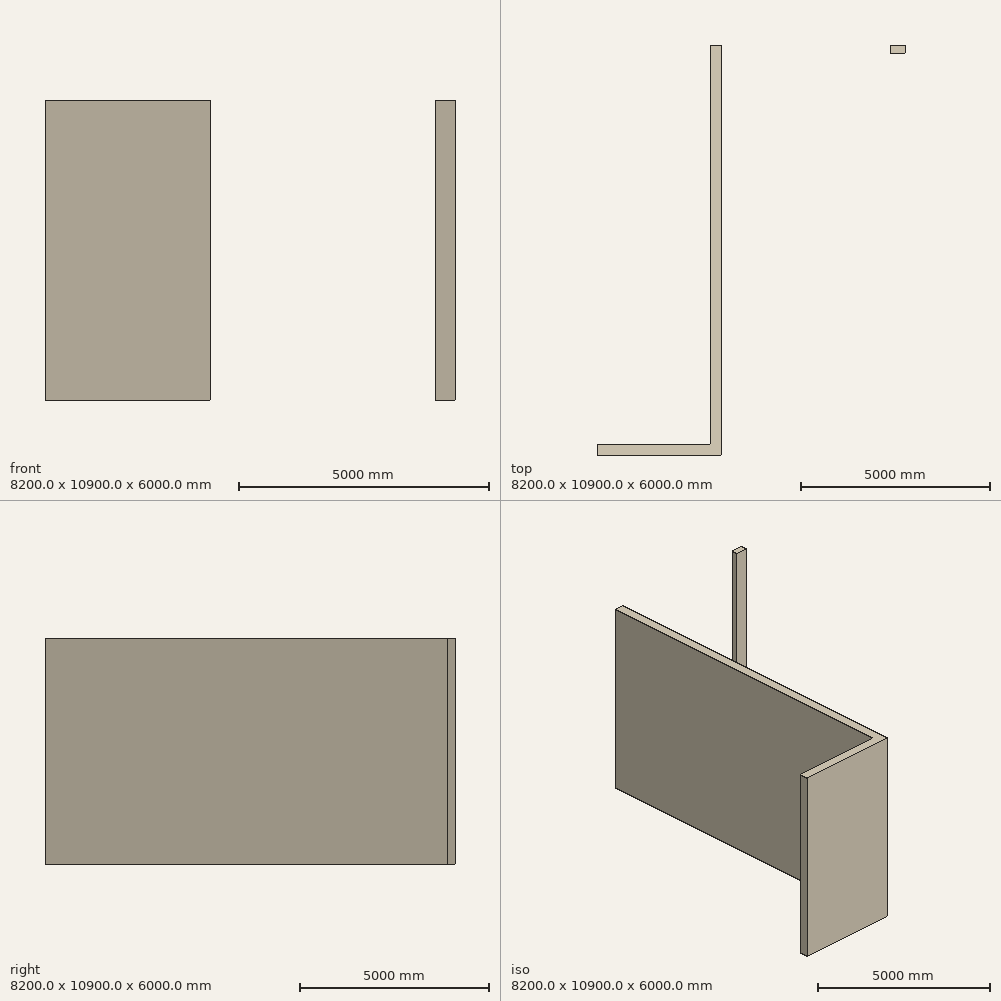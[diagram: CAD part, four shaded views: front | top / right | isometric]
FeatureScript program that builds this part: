
annotation { "Feature Type Name" : "Feature", "Feature Type Description" : "" }
export const myFeature = defineFeature(function(context is Context, id is Id, definition is map)
    precondition{}
    {
        {
            var Q0;
            Q0=qCreatedBy(makeId("Top.planeOp"),FACE);
            var sketch = newSketch(context, id + "F0", { "sketchPlane" : qUnion([Q0])});
            skLineSegment(sketch, "E0", {"start": v(165.16, 485.18) * mm, "end": v(465.16, 485.18) * mm});
            skLineSegment(sketch, "E1", {"start": v(465.16, 485.18) * mm, "end": v(465.16, 11385.18) * mm});
            skLineSegment(sketch, "E2", {"start": v(465.16, 11385.18) * mm, "end": v(4965.16, 11385.18) * mm});
            skLineSegment(sketch, "E3", {"start": v(4965.16, 11385.18) * mm, "end": v(4965.16, 11185.18) * mm});
            skLineSegment(sketch, "E4", {"start": v(4965.16, 11185.18) * mm, "end": v(5365.16, 11185.18) * mm});
            skLineSegment(sketch, "E5", {"start": v(5365.16, 11185.18) * mm, "end": v(5365.16, 11385.18) * mm});
            skLineSegment(sketch, "E6", {"start": v(5365.16, 11385.18) * mm, "end": v(9865.16, 11385.18) * mm});
            skLineSegment(sketch, "E7", {"start": v(5365.16, 11385.18) * mm, "end": v(4965.16, 11385.18) * mm});
            skLineSegment(sketch, "E8", {"start": v(465.16, 11385.18) * mm, "end": v(165.16, 11385.18) * mm});
            skLineSegment(sketch, "E9", {"start": v(165.16, 11385.18) * mm, "end": v(165.16, 485.18) * mm});
            skLineSegment(sketch, "E10", {"start": v(9865.16, 11385.18) * mm, "end": v(9865.16, 485.18) * mm});
            skLineSegment(sketch, "E11", {"start": v(9865.16, 485.18) * mm, "end": v(465.16, 485.18) * mm});
            skLineSegment(sketch, "E12.bottom", {"start": v(165.16, 485.18) * mm, "end": v(-2834.84, 485.18) * mm});
            skLineSegment(sketch, "E12.top", {"start": v(165.16, 785.18) * mm, "end": v(-2834.84, 785.18) * mm});
            skLineSegment(sketch, "E12.left", {"start": v(165.16, 485.18) * mm, "end": v(165.16, 785.18) * mm});
            skLineSegment(sketch, "E12.right", {"start": v(-2834.84, 485.18) * mm, "end": v(-2834.84, 785.18) * mm});
            skLineSegment(sketch, "E13.bottom", {"start": v(465.16, 485.18) * mm, "end": v(1185.16, 485.18) * mm});
            skLineSegment(sketch, "E13.top", {"start": v(465.16, 10845.18) * mm, "end": v(1185.16, 10845.18) * mm});
            skLineSegment(sketch, "E13.left", {"start": v(465.16, 485.18) * mm, "end": v(465.16, 10845.18) * mm});
            skLineSegment(sketch, "E13.right", {"start": v(1185.16, 485.18) * mm, "end": v(1185.16, 10845.18) * mm});
            skLineSegment(sketch, "E14", {"start": v(5165.16, 11185.18) * mm, "end": v(5165.16, 485.18) * mm});
            skLineSegment(sketch, "E15.bottom", {"start": v(5165.16, 485.18) * mm, "end": v(4445.16, 485.18) * mm});
            skLineSegment(sketch, "E15.top", {"start": v(5165.16, 10845.18) * mm, "end": v(4445.16, 10845.18) * mm});
            skLineSegment(sketch, "E15.left", {"start": v(5165.16, 485.18) * mm, "end": v(5165.16, 10845.18) * mm});
            skLineSegment(sketch, "E15.right", {"start": v(4445.16, 485.18) * mm, "end": v(4445.16, 10845.18) * mm});
            skSolve(sketch);
        }
        {
            var Q0;
            Q0=makeQuery(id+"F0.imprint","IMPRINT",FACE,{"disambiguationData":[TD([[makeQuery(id+"F0.imprint","IMPRINT",EDGE,{"derivedFrom":sQuery(id+"F0.wireOp",EDGE,"E0")}),1.0]])]});
            extrude(context, id + "F1", {"entities" : qUnion([Q0]), "depth" : 6000 * mm, "offsetDistance" : 25 * mm});
        }
        {
            var Q0;
            Q0=makeQuery(id+"F0.imprint","IMPRINT",FACE,{"disambiguationData":[TD([[makeQuery(id+"F0.imprint","IMPRINT",EDGE,{"derivedFrom":sQuery(id+"F0.wireOp",EDGE,"E12.bottom")}),-1.0]])]});
            extrude(context, id + "F2", {"entities" : qUnion([Q0]), "operationType" : NewBodyOperationType.ADD, "depth" : 6000 * mm, "offsetDistance" : 25 * mm});
        }
        {
            var Q0;
            Q0=makeQuery(id+"F0.imprint","IMPRINT",FACE,{"disambiguationData":[TD([[makeQuery(id+"F0.imprint","IMPRINT",EDGE,{"derivedFrom":sQuery(id+"F0.wireOp",EDGE,"E3")}),1.0]])]});
            extrude(context, id + "F3", {"entities" : qUnion([Q0]), "depth" : 6000 * mm, "offsetDistance" : 25 * mm});
        }
    });
